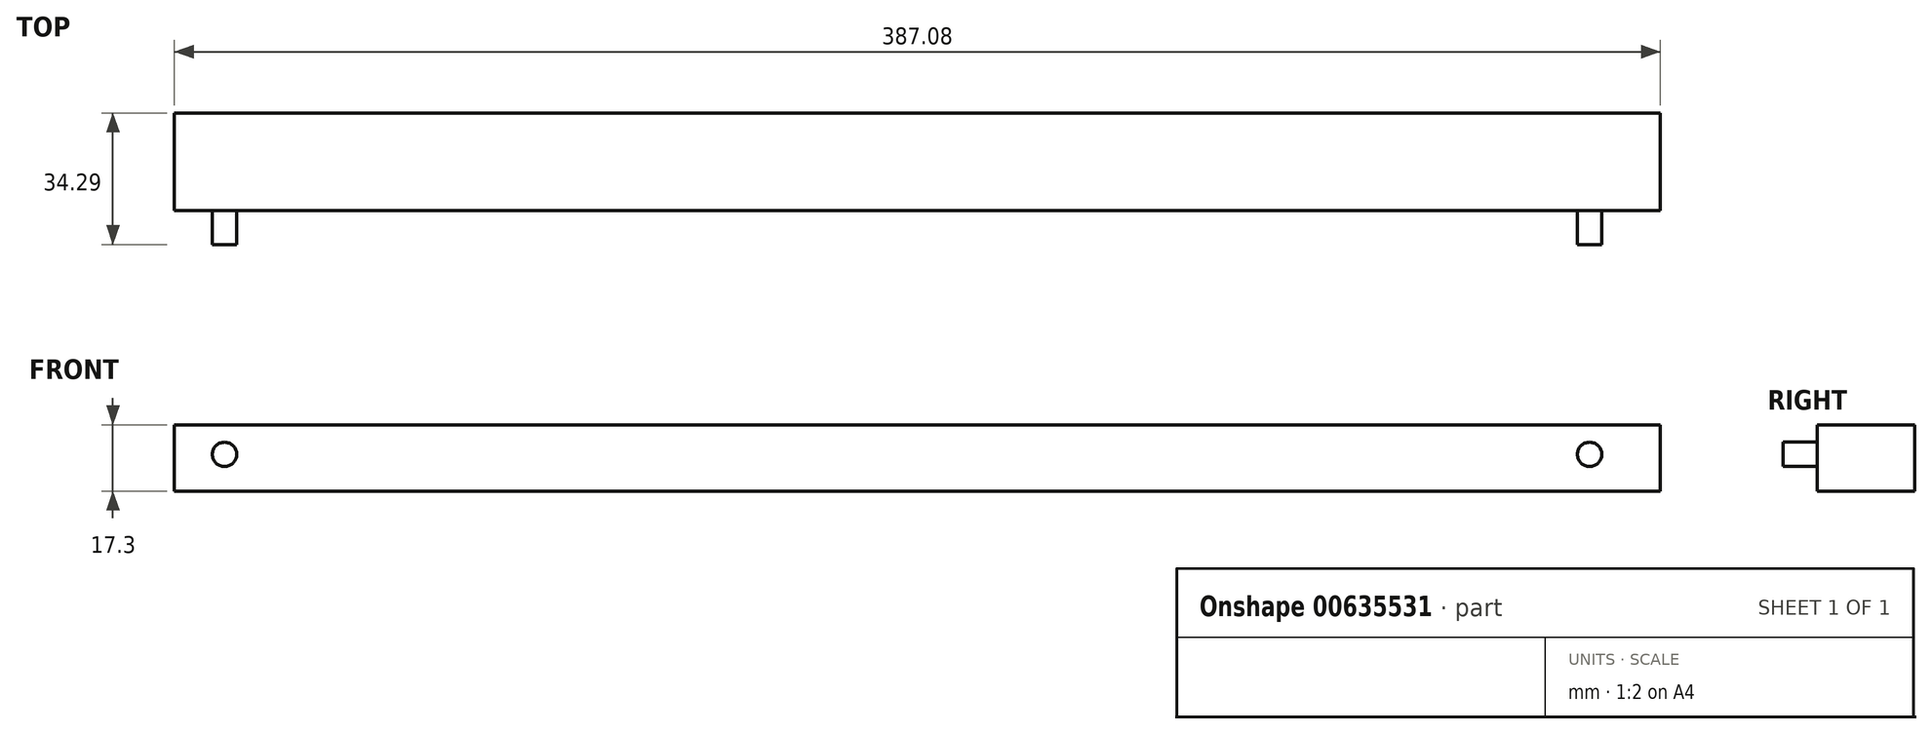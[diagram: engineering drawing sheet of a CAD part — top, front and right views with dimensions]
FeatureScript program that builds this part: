
annotation { "Feature Type Name" : "Feature", "Feature Type Description" : "" }
export const myFeature = defineFeature(function(context is Context, id is Id, definition is map)
    precondition{}
    {
        {
            var Q0;
            Q0=qCreatedBy(makeId("Front.planeOp"),FACE);
            var sketch = newSketch(context, id + "F0", { "sketchPlane" : qUnion([Q0])});
            skCircle(sketch, "E0", {"center": v(-72.74, 0) * mm, "radius": 3.18 * mm});
            skCircle(sketch, "E1", {"center": v(282.86, 0) * mm, "radius": 3.18 * mm});
            skLineSegment(sketch, "E2.bottom", {"start": v(-85.8, 7.69) * mm, "end": v(301.29, 7.69) * mm});
            skLineSegment(sketch, "E2.top", {"start": v(-85.8, -9.61) * mm, "end": v(301.29, -9.61) * mm});
            skLineSegment(sketch, "E2.left", {"start": v(-85.8, 7.69) * mm, "end": v(-85.8, -9.61) * mm});
            skLineSegment(sketch, "E2.right", {"start": v(301.29, 7.69) * mm, "end": v(301.29, -9.61) * mm});
            skSolve(sketch);
        }
        {
            var Q0;
            Q0=makeQuery(id+"F0.imprint","IMPRINT",FACE,{"disambiguationData":[TD([[makeQuery(id+"F0.imprint","IMPRINT",EDGE,{"derivedFrom":sQuery(id+"F0.wireOp",EDGE,"E0")}),-1.0]])]});
            var Q1;
            Q1=makeQuery(id+"F0.imprint","IMPRINT",FACE,{"disambiguationData":[TD([[makeQuery(id+"F0.imprint","IMPRINT",EDGE,{"derivedFrom":sQuery(id+"F0.wireOp",EDGE,"E0")}),1.0]])]});
            var Q2;
            Q2=makeQuery(id+"F0.imprint","IMPRINT",FACE,{"disambiguationData":[TD([[makeQuery(id+"F0.imprint","IMPRINT",EDGE,{"derivedFrom":sQuery(id+"F0.wireOp",EDGE,"E1")}),1.0]])]});
            extrude(context, id + "F1", {"entities" : qUnion([Q0, Q1, Q2]), "oppositeDirection" : true, "depth" : 25.4 * mm, "offsetDistance" : 25.4 * mm});
        }
        {
            var Q0;
            Q0=makeQuery(id+"F0.imprint","IMPRINT",FACE,{"disambiguationData":[TD([[makeQuery(id+"F0.imprint","IMPRINT",EDGE,{"derivedFrom":sQuery(id+"F0.wireOp",EDGE,"E0")}),1.0]])]});
            var Q1;
            Q1=makeQuery(id+"F0.imprint","IMPRINT",FACE,{"disambiguationData":[TD([[makeQuery(id+"F0.imprint","IMPRINT",EDGE,{"derivedFrom":sQuery(id+"F0.wireOp",EDGE,"E1")}),1.0]])]});
            extrude(context, id + "F2", {"entities" : qUnion([Q0, Q1]), "operationType" : NewBodyOperationType.ADD, "depth" : 8.9 * mm, "offsetDistance" : 25.4 * mm});
        }
    });
